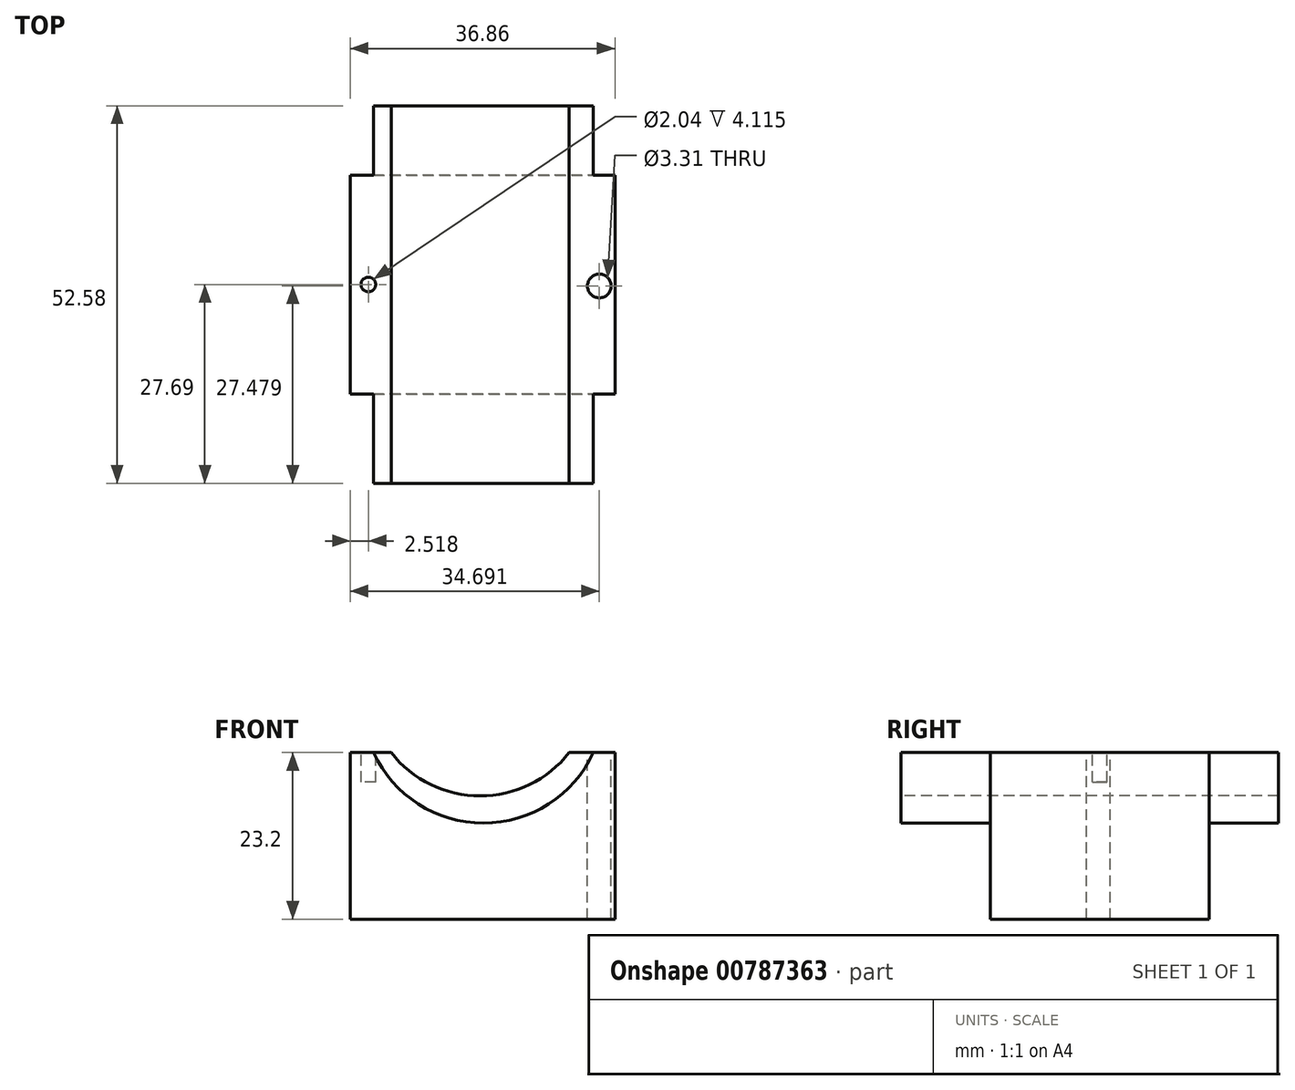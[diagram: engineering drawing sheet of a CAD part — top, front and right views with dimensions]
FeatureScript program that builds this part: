
annotation { "Feature Type Name" : "Feature", "Feature Type Description" : "" }
export const myFeature = defineFeature(function(context is Context, id is Id, definition is map)
    precondition{}
    {
        {
            var Q0;
            Q0=qCreatedBy(makeId("Front.planeOp"),FACE);
            var sketch = newSketch(context, id + "F0", { "sketchPlane" : qUnion([Q0])});
            skLineSegment(sketch, "E0.bottom", {"start": v(0, 0) * mm, "end": v(-36.86, 0) * mm});
            skLineSegment(sketch, "E0.top", {"start": v(0, 23.2) * mm, "end": v(-36.86, 23.2) * mm});
            skLineSegment(sketch, "E0.left", {"start": v(0, 0) * mm, "end": v(0, 23.2) * mm});
            skLineSegment(sketch, "E0.right", {"start": v(-36.86, 0) * mm, "end": v(-36.86, 23.2) * mm});
            skSolve(sketch);
        }
        {
            var Q0;
            Q0 = qSketchRegion(id + "F0", true);
            extrude(context, id + "F1", {"entities" : qUnion([Q0]), "depth" : 30.48 * mm, "offsetDistance" : 25.4 * mm});
        }
        {
            var Q0;
            Q0=makeQuery(id+"F1.opExtrude","CAP_FACE",FACE,{"disambiguationData":[OSD([sQuery(id+"F0.wireOp",EDGE,"E0.bottom"),sQuery(id+"F0.wireOp",EDGE,"E0.top"),sQuery(id+"F0.wireOp",EDGE,"E0.left"),sQuery(id+"F0.wireOp",EDGE,"E0.right")])],"isStart":false});
            var sketch = newSketch(context, id + "F2", { "sketchPlane" : qUnion([Q0])});
            skArc(sketch, "E1", {"start": v(-31.18, 23.2) * mm, "mid": v(-18.77, 17.16) * mm, "end": v(-6.36, 23.2) * mm});
            skLineSegment(sketch, "E2", {"start": v(-31.18, 23.2) * mm, "end": v(-33.62, 23.2) * mm});
            skLineSegment(sketch, "E3", {"start": v(-6.36, 23.2) * mm, "end": v(-3.01, 23.2) * mm});
            skArc(sketch, "E4", {"start": v(-33.62, 23.2) * mm, "mid": v(-18.32, 13.37) * mm, "end": v(-3.01, 23.2) * mm});
            skSolve(sketch);
        }
        {
            var Q0;
            Q0=makeQuery(id+"F2.imprint","IMPRINT",FACE,{"disambiguationData":[TD([[makeQuery(id+"F2.imprint","IMPRINT",EDGE,{"derivedFrom":sQuery(id+"F2.wireOp",EDGE,"E1")}),-1.0]])]});
            extrude(context, id + "F3", {"entities" : qUnion([Q0]), "operationType" : NewBodyOperationType.ADD, "oppositeDirection" : true, "depth" : 40.13 * mm, "offsetDistance" : 25.4 * mm});
        }
        {
            var Q0;
            Q0=makeQuery(id+"F3.opExtrude","CAP_FACE",FACE,{"disambiguationData":[OSD([sQuery(id+"F2.wireOp",EDGE,"E1"),sQuery(id+"F2.wireOp",EDGE,"E2"),sQuery(id+"F2.wireOp",EDGE,"E3"),sQuery(id+"F2.wireOp",EDGE,"E4")])],"isStart":false});
            extrude(context, id + "F4", {"entities" : qUnion([Q0]), "operationType" : NewBodyOperationType.ADD, "oppositeDirection" : true, "depth" : 52.58 * mm, "offsetDistance" : 25.4 * mm});
        }
        {
            var Q0;
            {var subQ2=sQuery(id+"F0.wireOp",EDGE,"E0.top");Q0=makeQuery(id+"F4.boolean.opBoolean","SPLIT",FACE,{"disambiguationData":[TD([makeQuery(id+"F4.opExtrude","SWEPT_FACE",FACE,{"disambiguationData":[OSD([sQuery(id+"F2.wireOp",EDGE,"E1")])]})])],"derivedFrom":makeQuery(id+"F1.opExtrude","CAP_FACE",FACE,{"disambiguationData":[OSD([sQuery(id+"F0.wireOp",EDGE,"E0.bottom"),subQ2,sQuery(id+"F0.wireOp",EDGE,"E0.left"),sQuery(id+"F0.wireOp",EDGE,"E0.right")])],"isStart":false})});}
            extrude(context, id + "F5", {"entities" : qUnion([Q0]), "operationType" : NewBodyOperationType.REMOVE, "oppositeDirection" : true, "depth" : 77.98 * mm, "offsetDistance" : 25.4 * mm});
        }
        {
            var Q0;
            {var subQ1=sQuery(id+"F0.wireOp",EDGE,"E0.right");var subQ3=sQuery(id+"F0.wireOp",EDGE,"E0.top");var subQ6=sQuery(id+"F2.wireOp",EDGE,"E3");var subQ7=sQuery(id+"F2.wireOp",EDGE,"E2");Q0=makeQuery(id+"F5.boolean.opBoolean","SPLIT",FACE,{"disambiguationData":[TD([makeQuery(id+"F1.opExtrude","SWEPT_FACE",FACE,{"disambiguationData":[OSD([subQ1])]})])],"derivedFrom":makeQuery(id+"F4.boolean.opBoolean","MERGE",FACE,{"derivedFrom":[makeQuery(id+"F3.boolean.opBoolean","MERGE",FACE,{"derivedFrom":[makeQuery(id+"F1.opExtrude","SWEPT_FACE",FACE,{"disambiguationData":[OSD([subQ3])]}),makeQuery(id+"F3.opExtrude","SWEPT_FACE",FACE,{"disambiguationData":[OSD([subQ7])]}),makeQuery(id+"F3.opExtrude","SWEPT_FACE",FACE,{"disambiguationData":[OSD([subQ6])]})]}),makeQuery(id+"F4.opExtrude","SWEPT_FACE",FACE,{"disambiguationData":[OSD([subQ7])]}),makeQuery(id+"F4.opExtrude","SWEPT_FACE",FACE,{"disambiguationData":[OSD([subQ6])]})]})});}
            var sketch = newSketch(context, id + "F6", { "sketchPlane" : qUnion([Q0])});
            skCircle(sketch, "E5", {"center": v(-34.34, -15.24) * mm, "radius": 1.02 * mm});
            skPoint(sketch, "E5.centerSnap0", {"position": v(-36.86, -15.24) * mm});
            skSolve(sketch);
        }
        {
            var Q0;
            Q0 = qSketchRegion(id + "F6", true);
            extrude(context, id + "F7", {"entities" : qUnion([Q0]), "operationType" : NewBodyOperationType.REMOVE, "oppositeDirection" : true, "depth" : 4.11 * mm, "offsetDistance" : 25.4 * mm});
        }
        {
            var Q0;
            {var subQ2=sQuery(id+"F0.wireOp",EDGE,"E0.left");var subQ3=sQuery(id+"F0.wireOp",EDGE,"E0.top");var subQ6=sQuery(id+"F2.wireOp",EDGE,"E3");var subQ7=sQuery(id+"F2.wireOp",EDGE,"E2");Q0=makeQuery(id+"F5.boolean.opBoolean","SPLIT",FACE,{"disambiguationData":[TD([makeQuery(id+"F1.opExtrude","SWEPT_FACE",FACE,{"disambiguationData":[OSD([subQ2])]})])],"derivedFrom":makeQuery(id+"F4.boolean.opBoolean","MERGE",FACE,{"derivedFrom":[makeQuery(id+"F3.boolean.opBoolean","MERGE",FACE,{"derivedFrom":[makeQuery(id+"F1.opExtrude","SWEPT_FACE",FACE,{"disambiguationData":[OSD([subQ3])]}),makeQuery(id+"F3.opExtrude","SWEPT_FACE",FACE,{"disambiguationData":[OSD([subQ7])]}),makeQuery(id+"F3.opExtrude","SWEPT_FACE",FACE,{"disambiguationData":[OSD([subQ6])]})]}),makeQuery(id+"F4.opExtrude","SWEPT_FACE",FACE,{"disambiguationData":[OSD([subQ7])]}),makeQuery(id+"F4.opExtrude","SWEPT_FACE",FACE,{"disambiguationData":[OSD([subQ6])]})]})});}
            var sketch = newSketch(context, id + "F8", { "sketchPlane" : qUnion([Q0])});
            skCircle(sketch, "E6", {"center": v(-2.17, -15.45) * mm, "radius": 1.65 * mm});
            skSolve(sketch);
        }
        {
            var Q0;
            Q0=makeQuery(id+"F8.imprint","IMPRINT",FACE,{"disambiguationData":[TD([[makeQuery(id+"F8.imprint","IMPRINT",EDGE,{"derivedFrom":sQuery(id+"F8.wireOp",EDGE,"E6")}),1.0]])]});
            extrude(context, id + "F9", {"entities" : qUnion([Q0]), "operationType" : NewBodyOperationType.REMOVE, "oppositeDirection" : true, "depth" : 43.9 * mm, "offsetDistance" : 25.4 * mm});
        }
    });
